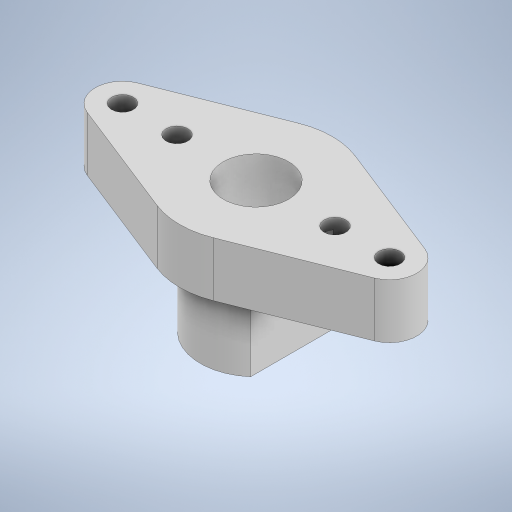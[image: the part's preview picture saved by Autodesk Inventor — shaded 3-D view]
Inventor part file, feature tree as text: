
AUTODESK INVENTOR PART (.ipt)
format: ipt  version: 2023 (Build 270158000, 158)  size: 289,792 bytes
history: native  units: mm
features: extrude x4, sketch x2, other x1
ambient origin geometry x8: Origin, YZ Plane, XZ Plane, XY Plane, X Axis, Y Axis, Z Axis, Center Point
bodies: Body1 (feature_tree)
feature tree (7):
  other  "ソリッド1"
  extrude  "押し出し1"  Depth=7.0mm
  sketch  "スケッチ2"
  extrude  "押し出し2"  Depth=1.6mm
  extrude  "押し出し3"  Depth=1.6mm
  extrude  "押し出し4"  Depth=7.0mm TaperAngle=0.0deg
  sketch  "スケッチ1"
